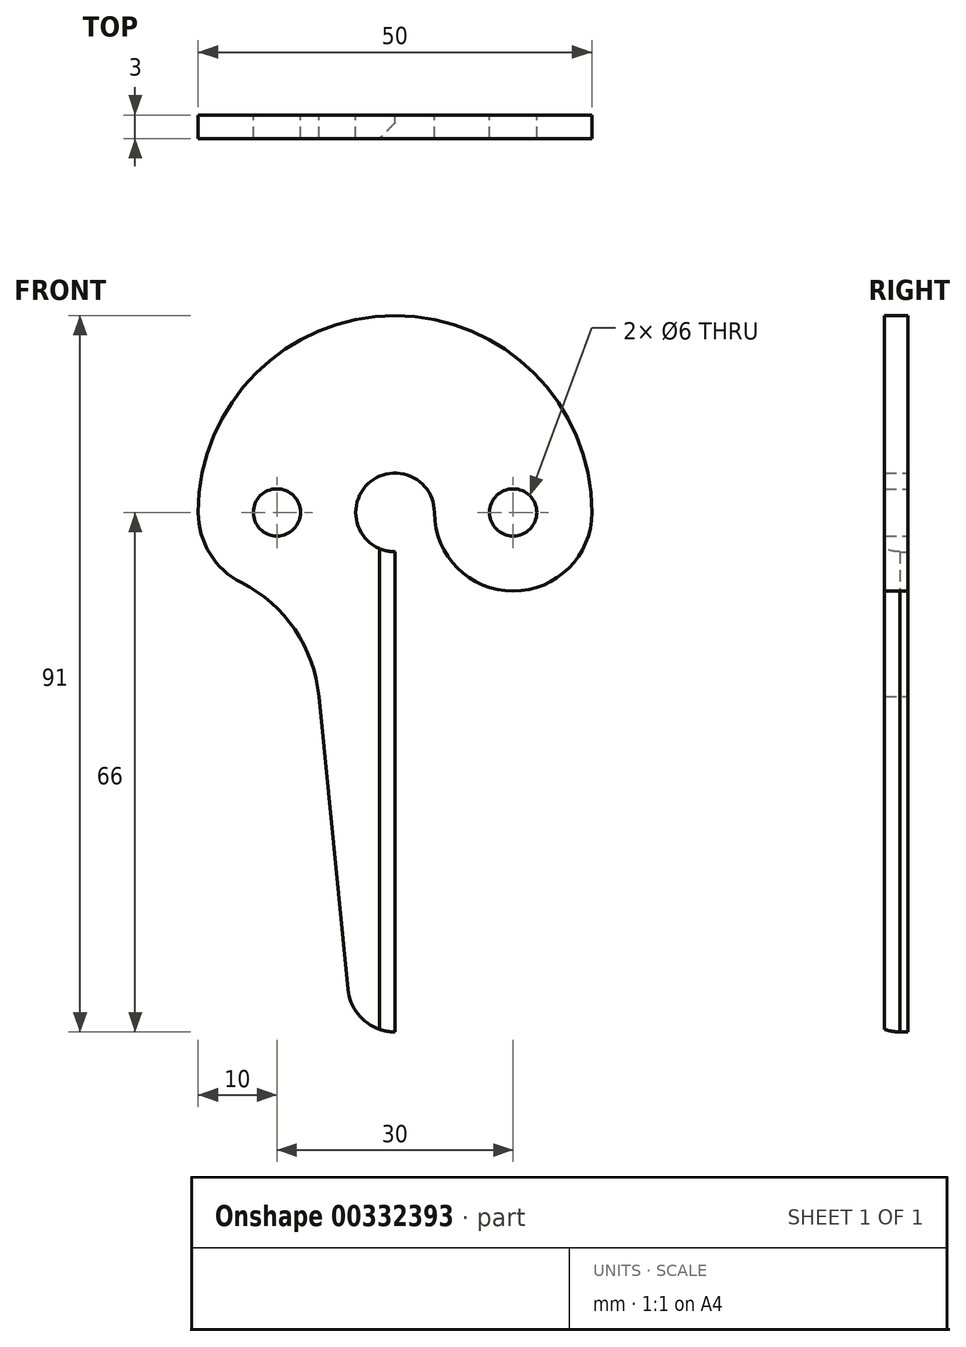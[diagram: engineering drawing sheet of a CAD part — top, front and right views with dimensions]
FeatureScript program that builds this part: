
annotation { "Feature Type Name" : "Feature", "Feature Type Description" : "" }
export const myFeature = defineFeature(function(context is Context, id is Id, definition is map)
    precondition{}
    {
        {
            var Q0;
            Q0=qCreatedBy(makeId("Front.planeOp"),FACE);
            var sketch = newSketch(context, id + "F0", { "sketchPlane" : qUnion([Q0])});
            skArc(sketch, "E0", {"start": v(25, 0) * mm, "mid": v(0, 25) * mm, "end": v(-25, 0) * mm});
            skPoint(sketch, "E1", {"position": v(-15, 0) * mm});
            skPoint(sketch, "E2", {"position": v(15, 0) * mm});
            skArc(sketch, "E3", {"start": v(5, 0) * mm, "mid": v(-3.54, 3.54) * mm, "end": v(0, -5) * mm});
            skCircle(sketch, "E4", {"center": v(-15, 0) * mm, "radius": 3 * mm});
            skCircle(sketch, "E5", {"center": v(15, 0) * mm, "radius": 3 * mm});
            skPoint(sketch, "E6", {"position": v(-27.6, -25) * mm});
            skArc(sketch, "E7", {"start": v(-9.68, -23.4) * mm, "mid": v(-12.72, -14.89) * mm, "end": v(-19.5, -8.93) * mm});
            skPoint(sketch, "E8", {"position": v(0, -60) * mm});
            skArc(sketch, "E9", {"start": v(-5.97, -60.6) * mm, "mid": v(-4.03, -64.45) * mm, "end": v(0, -66) * mm});
            skLineSegment(sketch, "E10", {"start": v(-9.72, -23.03) * mm, "end": v(-5.97, -60.6) * mm});
            skLineSegment(sketch, "E11", {"start": v(0, 0) * mm, "end": v(0, -60) * mm});
            skArc(sketch, "E12", {"start": v(5, 0) * mm, "mid": v(15, -10) * mm, "end": v(25, 0) * mm});
            skArc(sketch, "E13", {"start": v(-25, 0) * mm, "mid": v(-23.52, -5.24) * mm, "end": v(-19.5, -8.93) * mm});
            skLineSegment(sketch, "E14", {"start": v(0, -60) * mm, "end": v(0, -66) * mm});
            skSolve(sketch);
        }
        {
            var Q0;
            Q0=makeQuery(id+"F0.imprint","IMPRINT",FACE,{"disambiguationData":[TD([[makeQuery(id+"F0.imprint","IMPRINT",EDGE,{"derivedFrom":sQuery(id+"F0.wireOp",EDGE,"E0")}),1.0]])]});
            extrude(context, id + "F1", {"entities" : qUnion([Q0]), "depth" : 3 * mm});
        }
        {
            var Q0;
            Q0=makeQuery(id+"F1.opExtrude","CAP_EDGE",EDGE,{"disambiguationData":[OSD([sQuery(id+"F0.wireOp",EDGE,"E11"),sQuery(id+"F0.wireOp",EDGE,"E14")])],"isStart":false});
            chamfer(context, id + "F2", {"entities" : qUnion([Q0]), "width" : 2 * mm, "tangentPropagation" : true});
        }
    });
